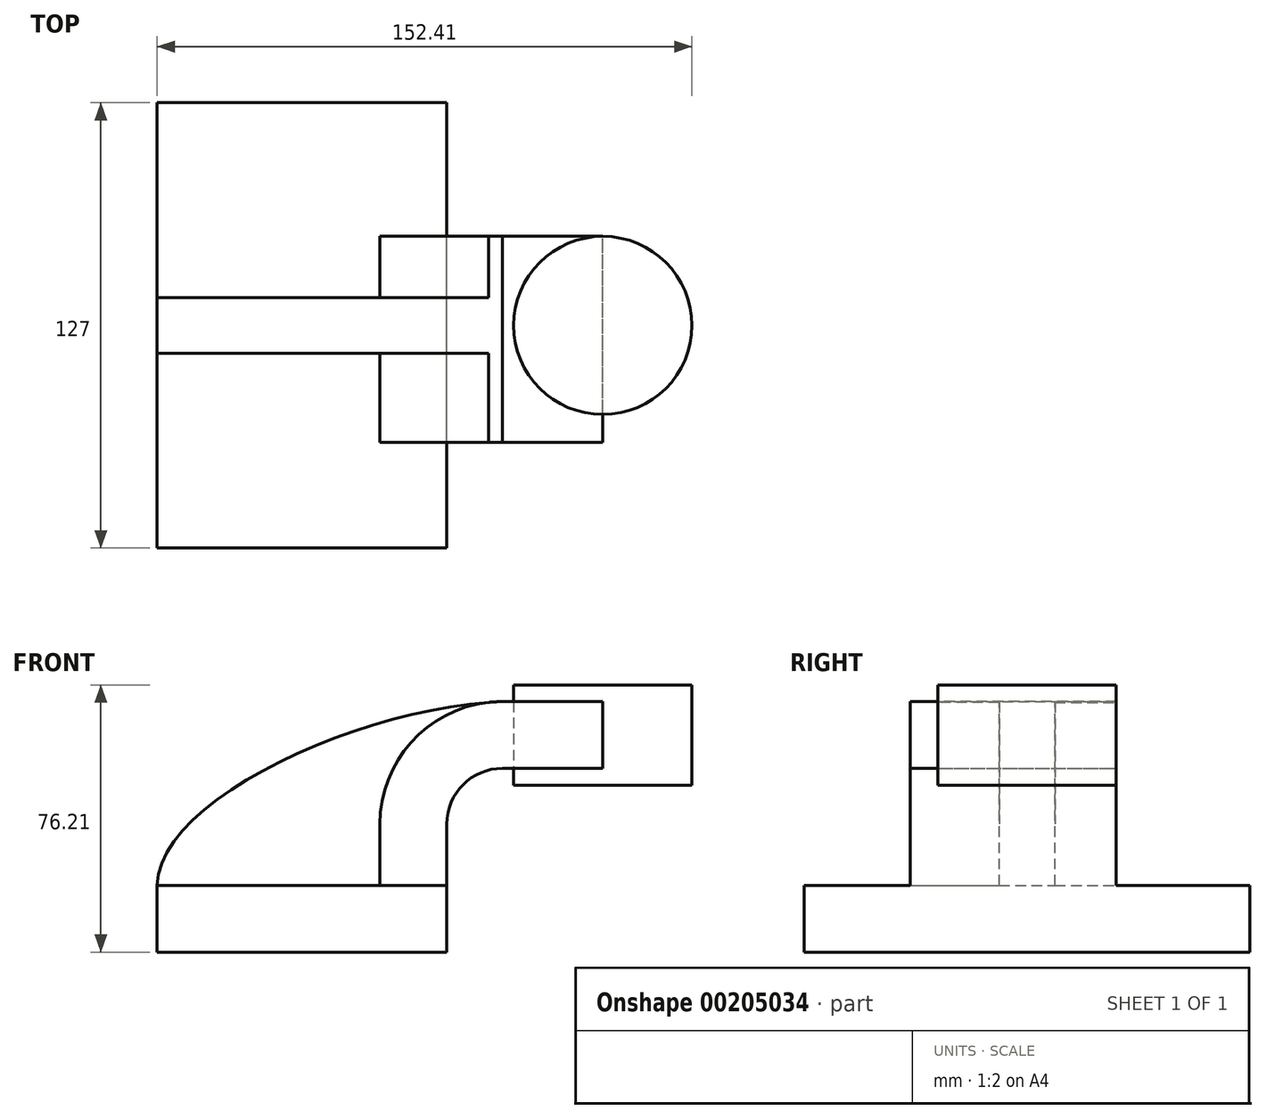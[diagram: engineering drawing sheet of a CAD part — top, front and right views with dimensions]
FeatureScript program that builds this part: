
annotation { "Feature Type Name" : "Feature", "Feature Type Description" : "" }
export const myFeature = defineFeature(function(context is Context, id is Id, definition is map)
    precondition{}
    {
        {
            var Q0;
            Q0=qCreatedBy(makeId("Front.planeOp"),FACE);
            var sketch = newSketch(context, id + "F0", { "sketchPlane" : qUnion([Q0])});
            skLineSegment(sketch, "E0.bottom", {"start": v(-41.28, 9.53) * mm, "end": v(41.28, 9.53) * mm});
            skLineSegment(sketch, "E0.top", {"start": v(-41.28, -9.53) * mm, "end": v(41.28, -9.53) * mm});
            skLineSegment(sketch, "E0.left", {"start": v(-41.28, 9.53) * mm, "end": v(-41.28, -9.53) * mm});
            skLineSegment(sketch, "E0.right", {"start": v(41.28, 9.53) * mm, "end": v(41.28, -9.53) * mm});
            skPoint(sketch, "E0.middle", {"position": v(0, 0) * mm});
            skLineSegment(sketch, "E1.bottom", {"start": v(111.12, 66.67) * mm, "end": v(60.32, 66.67) * mm});
            skLineSegment(sketch, "E1.top", {"start": v(111.12, 38.1) * mm, "end": v(60.32, 38.1) * mm});
            skLineSegment(sketch, "E1.left", {"start": v(111.12, 66.68) * mm, "end": v(111.13, 38.1) * mm});
            skLineSegment(sketch, "E1.right", {"start": v(60.32, 66.68) * mm, "end": v(60.32, 38.1) * mm});
            skPoint(sketch, "E1.middle", {"position": v(85.72, 52.39) * mm});
            skLineSegment(sketch, "E2", {"start": v(41.27, 9.52) * mm, "end": v(41.27, 27) * mm});
            skArc(sketch, "E3", {"start": v(41.28, 27) * mm, "mid": v(45.92, 38.23) * mm, "end": v(57.15, 42.88) * mm});
            skLineSegment(sketch, "E4", {"start": v(57.15, 42.88) * mm, "end": v(85.73, 42.88) * mm});
            skLineSegment(sketch, "E5.0", {"start": v(57.15, 61.93) * mm, "end": v(85.73, 61.93) * mm});
            skArc(sketch, "E5.1", {"start": v(22.23, 27) * mm, "mid": v(32.45, 51.7) * mm, "end": v(57.15, 61.93) * mm});
            skLineSegment(sketch, "E5.2", {"start": v(22.23, 9.52) * mm, "end": v(22.23, 27) * mm});
            skLineSegment(sketch, "E6", {"start": v(85.72, 38.1) * mm, "end": v(85.72, 66.67) * mm});
            skFitSpline(sketch, "E7", {"points": [v(-41.28, 9.52) * mm, v(57.15, 61.93) * mm], "startDerivative": vector(1.87, 74.15) * mm, "endDerivative": vector(120.96, 4.68) * mm});
            skSolve(sketch);
        }
        {
            var Q0;
            Q0=makeQuery(id+"F0.imprint","IMPRINT",FACE,{"disambiguationData":[TD([[makeQuery(id+"F0.imprint","IMPRINT",EDGE,{"derivedFrom":sQuery(id+"F0.wireOp",EDGE,"E0.top")}),1.0]])]});
            extrude(context, id + "F1", {"entities" : qUnion([Q0]), "endBound" : BoundingType.SYMMETRIC, "depth" : 127 * mm});
        }
        {
            var Q0;
            {var subQ0=sQuery(id+"F0.wireOp",EDGE,"E5.0");var subQ1=sQuery(id+"F0.wireOp",EDGE,"E1.right");var subQ2=makeQuery(id+"F0.imprint","INTERSECT",VERTEX,{"derivedFrom":[subQ1,subQ0]});Q0=makeQuery(id+"F0.imprint","IMPRINT",FACE,{"disambiguationData":[TD([[makeQuery(id+"F0.imprint","IMPRINT",EDGE,{"disambiguationData":[TD([[subQ2,-1.0]])],"derivedFrom":subQ1}),1.0]])]});}
            var Q1;
            {var subQ1=sQuery(id+"F0.wireOp",EDGE,"E2");Q1=makeQuery(id+"F0.imprint","IMPRINT",FACE,{"disambiguationData":[TD([[makeQuery(id+"F0.imprint","IMPRINT",EDGE,{"derivedFrom":subQ1}),1.0]])]});}
            extrude(context, id + "F2", {"entities" : qUnion([Q0, Q1]), "operationType" : NewBodyOperationType.ADD, "endBound" : BoundingType.SYMMETRIC, "depth" : 50.8 * mm});
        }
        {
            var Q0;
            {var subQ3=sQuery(id+"F0.wireOp",EDGE,"E5.2");Q0=makeQuery(id+"F0.imprint","IMPRINT",FACE,{"disambiguationData":[TD([[makeQuery(id+"F0.imprint","IMPRINT",EDGE,{"derivedFrom":subQ3}),1.0]])]});}
            var Q1;
            Q1=makeQuery(id+"F2.opExtrude","CAP_FACE",FACE,{"disambiguationData":[OSD([sQuery(id+"F0.wireOp",EDGE,"E0.bottom"),sQuery(id+"F0.wireOp",EDGE,"E2"),sQuery(id+"F0.wireOp",EDGE,"E3"),sQuery(id+"F0.wireOp",EDGE,"E4"),sQuery(id+"F0.wireOp",EDGE,"E5.0"),sQuery(id+"F0.wireOp",EDGE,"E6"),sQuery(id+"F0.wireOp",EDGE,"E7")])],"isStart":false});
            extrude(context, id + "F3", {"entities" : qUnion([Q0, Q1]), "operationType" : NewBodyOperationType.ADD, "endBound" : BoundingType.SYMMETRIC, "depth" : 15.88 * mm});
        }
        {
            var Q0;
            {var subQ0=sQuery(id+"F0.wireOp",EDGE,"E1.left");Q0=makeQuery(id+"F0.imprint","IMPRINT",FACE,{"disambiguationData":[TD([[makeQuery(id+"F0.imprint","IMPRINT",EDGE,{"derivedFrom":subQ0}),-1.0]])]});}
            var Q1;
            Q1=sQuery(id+"F0.wireOp",EDGE,"E6");
            revolve(context, id + "F4", {"entities" : qUnion([Q0]), "axis" : qUnion([Q1]), "revolveType" : RevolveType.FULL});
        }
    });
